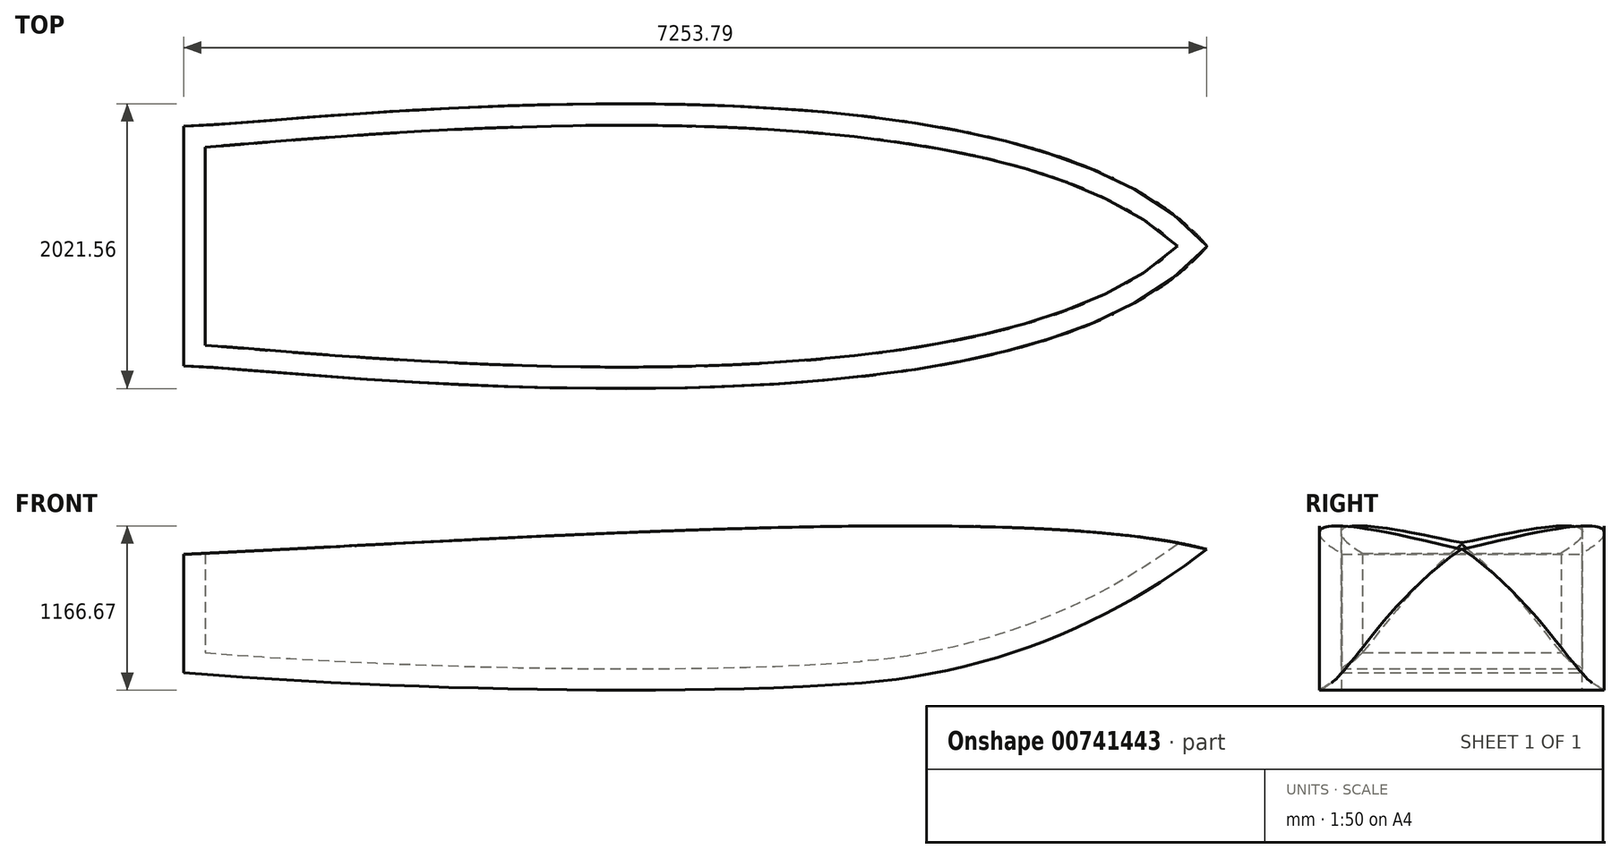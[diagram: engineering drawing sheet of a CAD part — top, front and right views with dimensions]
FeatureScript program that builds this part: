
annotation { "Feature Type Name" : "Feature", "Feature Type Description" : "" }
export const myFeature = defineFeature(function(context is Context, id is Id, definition is map)
    precondition{}
    {
        {
            var Q0;
            Q0=qCreatedBy(makeId("Front.planeOp"),FACE);
            var sketch = newSketch(context, id + "F0", { "sketchPlane" : qUnion([Q0])});
            skFitSpline(sketch, "E0", {"points": [v(2286.14, 213.69) * mm, v(-3265.45, 173.92) * mm], "startDerivative": vector(-1822.5, -641.06) * mm, "endDerivative": vector(-6240.83, 521.77) * mm});
            skArc(sketch, "E1.filletArc", {"start": v(1546.6, 99.73) * mm, "mid": v(2838.74, 394.8) * mm, "end": v(3991.95, 1048.1) * mm});
            skLineSegment(sketch, "E2", {"start": v(-3265.45, 173.92) * mm, "end": v(-3275.83, 1012.12) * mm});
            skFitSpline(sketch, "E3", {"points": [v(-3275.83, 1012.12) * mm, v(3991.95, 1048.1) * mm], "startDerivative": vector(7179.52, 340.71) * mm, "endDerivative": vector(3700.93, -1010.33) * mm});
            skSolve(sketch);
        }
        {
            var Q0;
            Q0=qSketchRegion(id+"F0",true);
            extrude(context, id + "F1", {"entities" : qUnion([Q0]), "endBound" : BoundingType.SYMMETRIC, "depth" : 2032 * mm, "offsetDistance" : 25.4 * mm});
        }
        {
            var Q0;
            Q0=qCreatedBy(makeId("Top.planeOp"),FACE);
            var sketch = newSketch(context, id + "F2", { "sketchPlane" : qUnion([Q0])});
            skFitSpline(sketch, "E4", {"points": [v(-3261.84, -851.35) * mm, v(3995.55, 0) * mm], "startDerivative": vector(1071.73, 76.55) * mm, "endDerivative": vector(4050.3, 4753.19) * mm});
            skFitSpline(sketch, "E5.MirrorCS", {"points": [v(-3261.84, 851.35) * mm, v(3995.55, 0) * mm], "startDerivative": vector(1071.73, -76.55) * mm, "endDerivative": vector(4050.3, -4753.19) * mm});
            skLineSegment(sketch, "E6", {"start": v(-3261.84, 851.35) * mm, "end": v(-3261.84, -851.35) * mm});
            skSolve(sketch);
        }
        {
            var Q0;
            Q0=qSketchRegion(id+"F2",true);
            extrude(context, id + "F3", {"entities" : qUnion([Q0]), "operationType" : NewBodyOperationType.INTERSECT, "depth" : 1905 * mm, "offsetDistance" : 25.4 * mm});
        }
        {
            var Q0;
            Q0=makeQuery(id+"F1.opExtrude","SWEPT_FACE",FACE,{"disambiguationData":[OSD([sQuery(id+"F0.wireOp",EDGE,"E3")])]});
            shell(context, id + "F4", {"entities" : qUnion([Q0]), "thickness" : 152.4 * mm});
        }
    });
